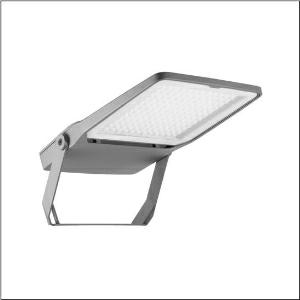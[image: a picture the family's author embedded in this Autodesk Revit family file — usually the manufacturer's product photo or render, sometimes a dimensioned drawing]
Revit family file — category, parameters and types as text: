
# Revit family: floodlight_fl_20_midi___pl61_5xa7682d3c1ac_fcc5
name_source: partatom
category: Lighting Fixtures
units: mm (PartAtom-declared; Revit-internal decimal feet)

## family parameters
Cut with Voids When Loaded = No
Host = Face
Light Source = No
Part Type = Normal
Room Calculation Point = No
Round Connector Dimension = Use Diameter
Shared = No

## types (1)
- --- (1 x LED 5000K / CRI = 70 (unbekannt), 18470 lm, 5000K)
    Apparent Load = 142 VA
    CIE Flux Codes = 33 65 98 100 100
    Color Rendering = 70
    Color Temperature = 5000K
    Default Elevation = 1800 mm
    Description = Floodlight FL 20 midi, floodlight, primary light control with lens, of plastic, primary optical cover: protective disc, of toughened safety glass, transparent, light distribution: PL61, light emission: direct distribution, primary light characteristic: asymmetric, installation type: surface-mounted, LED, High Power LED, rated luminous flux: 18.470lm, luminous efficacy: 130lm/W, light colour: 750, colour temperature: 5000K, control gear: ECG Plus, control: flexible luminous flux parameterisation, time-dependent luminous flux control, digital communication interface, power reduction, overheat protection, electronic power reduction, with terminal, 5-pole, max. 2.5mm², mains connection: 220..240V, AC, 50/60Hz, rated input power: 142W, LED unit, of diecast aluminium, powder-coated, Siteco® metallic grey (DB 702S), corrosivity category C5 mid according to DIN EN ISO 12944, incl. 1x M20 cable gland for cable Ø 6.5..12mm, length: 654mm, width: 450mm, height: 76mm, housing frame, of diecast aluminium, powder-coated, Siteco® metallic grey (DB 702S), mounting bracket, of steel, powder-coated, Siteco® metallic grey (DB 702S), DALI, protection rating (complete): IP66, insulation class (complete): insulation class II (safety insulation), certification: CE, ENEC, VDE, protection symbol: D, permissible operating ambient temperature: -40..+40°C, permissible operating ambient temperature for outdoor applications: -40..+50°C, standard: DIN EN 12944, packaging unit: 1 piece

Light Distribution: PL61
    Height = 76 mm
    Lamp = 1 x LED 5000K / CRI >= 70 (unbekannt)
    Lamp Light Flux = 18470 lm
    Lamp count = 1
    Length = 672 mm
    Luminous efficacy = 130 lm/W
    Manufacturer = Siteco
    ModVariant = No
    Model = 5XA7682D3C1AC
    Mounting Place = Wall
    Mounting Type = Surface mounted
    Number of Poles = 1
    OnlyDefault = Yes
    Power Factor = 1
    Product Name = Floodlight FL 20 midi | PL61
    Product group = floodlight | wall mounted
    ProductGroupID = 2001
    Protection Class = Protection class II
    Protection Degree = IP 66
    RLX_Detail_Level = 1
    RLX_Emergency_Light_Flux = 0 lm
    RLX_Emergency_Type = 0
    RLX_Emergency_Type_DB = No
    RlxData = <blob elided: 97649 chars, md5=e890e2d6>
    Socket = socket
    Standby Power = 0 W
    System Light Flux = 18470 lm
    System Power = 142 W
    Type Comments = factory setting: luminous flux: 100 % | dim-lin: 254 | 489 mA
    Type Image = l_1005943.jpg
    URL = http://relux.com
    VarID = @adj_147171
    Voltage = 0 V
    Weight = 0.00 kg
    Width = 450 mm

## geometry (parser evidence)
native form markers: Blend x4, Sweep x11
no freeform markers — native parametric forms only
